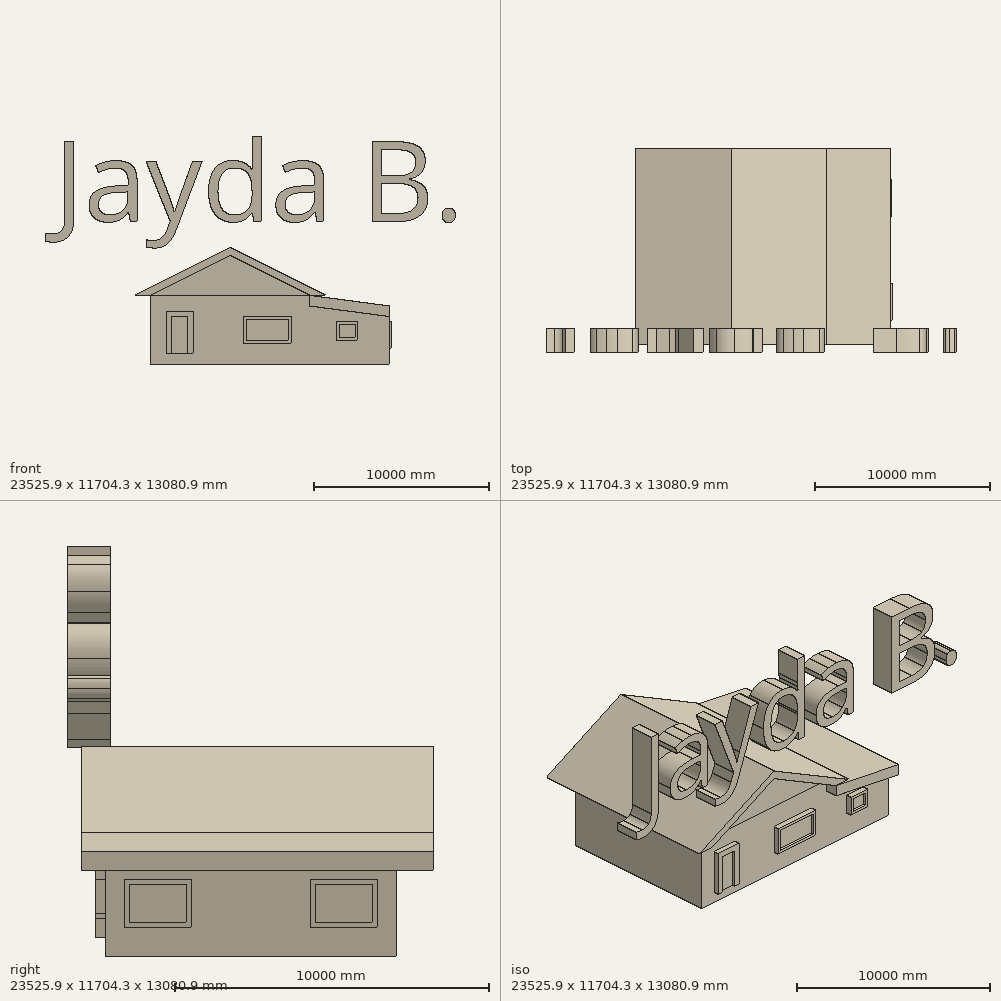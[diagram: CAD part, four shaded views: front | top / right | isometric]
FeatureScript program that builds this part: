
annotation { "Feature Type Name" : "Feature", "Feature Type Description" : "" }
export const myFeature = defineFeature(function(context is Context, id is Id, definition is map)
    precondition{}
    {
        {
            var Q0;
            Q0=qCreatedBy(makeId("Front.planeOp"),FACE);
            var sketch = newSketch(context, id + "F0", { "sketchPlane" : qUnion([Q0])});
            skLineSegment(sketch, "E0", {"start": v(0, 0) * mm, "end": v(-4572, 0) * mm});
            skLineSegment(sketch, "E1", {"start": v(0, 0) * mm, "end": v(4572, 0) * mm});
            skLineSegment(sketch, "E2", {"start": v(0, 0) * mm, "end": v(0, 2286) * mm});
            skLineSegment(sketch, "E3", {"start": v(-4572, 0) * mm, "end": v(0, 2286) * mm});
            skLineSegment(sketch, "E4", {"start": v(4572, 0) * mm, "end": v(0, 2286) * mm});
            skLineSegment(sketch, "E5", {"start": v(4572, 0) * mm, "end": v(5486.4, 0) * mm});
            skLineSegment(sketch, "E6", {"start": v(-4572, 0) * mm, "end": v(-5486.4, 0) * mm});
            skLineSegment(sketch, "E7", {"start": v(0, 2286) * mm, "end": v(0, 2743.2) * mm});
            skLineSegment(sketch, "E8", {"start": v(-5486.4, 0) * mm, "end": v(0, 2743.2) * mm});
            skLineSegment(sketch, "E9", {"start": v(5486.4, 0) * mm, "end": v(0, 2743.2) * mm});
            skLineSegment(sketch, "E10", {"start": v(-4572, 0) * mm, "end": v(-4572, -3352.8) * mm});
            skLineSegment(sketch, "E11", {"start": v(4572, 0) * mm, "end": v(4572, -3352.8) * mm});
            skLineSegment(sketch, "E12", {"start": v(4572, 0) * mm, "end": v(9144, -603.27) * mm});
            skLineSegment(sketch, "E13", {"start": v(-4572, -3352.8) * mm, "end": v(4572, -3352.8) * mm});
            skLineSegment(sketch, "E14", {"start": v(-4572, -3352.8) * mm, "end": v(-4572, -3962.4) * mm});
            skLineSegment(sketch, "E15", {"start": v(4572, -3352.8) * mm, "end": v(4572, -3962.4) * mm});
            skLineSegment(sketch, "E16", {"start": v(-4572, -3962.4) * mm, "end": v(4572, -3962.4) * mm});
            skLineSegment(sketch, "E17", {"start": v(-2438.4, -3352.8) * mm, "end": v(-2133.6, -3352.8) * mm});
            skLineSegment(sketch, "E18", {"start": v(-2438.4, -3352.8) * mm, "end": v(-2438.4, -1219.2) * mm});
            skLineSegment(sketch, "E19", {"start": v(-3657.6, -3352.8) * mm, "end": v(-3352.8, -3352.8) * mm});
            skLineSegment(sketch, "E20", {"start": v(-3352.8, -3352.8) * mm, "end": v(-3352.8, -1219.2) * mm});
            skLineSegment(sketch, "E21", {"start": v(-3352.8, -1219.2) * mm, "end": v(-2438.4, -1219.2) * mm});
            skLineSegment(sketch, "E22.0", {"start": v(-2133.6, -3352.8) * mm, "end": v(-2133.6, -914.4) * mm});
            skLineSegment(sketch, "E22.1", {"start": v(-3657.6, -914.4) * mm, "end": v(-2133.6, -914.4) * mm});
            skLineSegment(sketch, "E22.2", {"start": v(-3657.6, -3352.8) * mm, "end": v(-3657.6, -914.4) * mm});
            skLineSegment(sketch, "E23", {"start": v(9144, -603.27) * mm, "end": v(9144, -3346.47) * mm});
            skLineSegment(sketch, "E24", {"start": v(4572, -609.6) * mm, "end": v(9144, -1212.87) * mm});
            skLineSegment(sketch, "E25", {"start": v(9144, -3352.8) * mm, "end": v(9144, -3346.47) * mm});
            skLineSegment(sketch, "E26", {"start": v(4572, -3352.8) * mm, "end": v(9144, -3346.47) * mm});
            skLineSegment(sketch, "E27", {"start": v(4572, -3962.4) * mm, "end": v(9144, -3956.07) * mm});
            skLineSegment(sketch, "E28", {"start": v(9144, -3956.07) * mm, "end": v(9144, -3346.47) * mm});
            skLineSegment(sketch, "E29.bottom", {"start": v(6248.4, -1672.6) * mm, "end": v(7162.8, -1672.6) * mm});
            skLineSegment(sketch, "E29.top", {"start": v(6248.4, -2434.6) * mm, "end": v(7162.8, -2434.6) * mm});
            skLineSegment(sketch, "E29.left", {"start": v(6248.4, -1672.6) * mm, "end": v(6248.4, -2434.6) * mm});
            skLineSegment(sketch, "E29.right", {"start": v(7162.8, -1672.6) * mm, "end": v(7162.8, -2434.6) * mm});
            skLineSegment(sketch, "E30.0", {"start": v(6096, -1520.2) * mm, "end": v(7315.2, -1520.2) * mm});
            skLineSegment(sketch, "E30.1", {"start": v(6096, -1520.2) * mm, "end": v(6096, -2587) * mm});
            skLineSegment(sketch, "E30.2", {"start": v(6096, -2587) * mm, "end": v(7315.2, -2587) * mm});
            skLineSegment(sketch, "E30.3", {"start": v(7315.2, -1520.2) * mm, "end": v(7315.2, -2587) * mm});
            skLineSegment(sketch, "E31.bottom", {"start": v(914.4, -1371.6) * mm, "end": v(3352.8, -1371.6) * mm});
            skLineSegment(sketch, "E31.top", {"start": v(914.4, -2590.8) * mm, "end": v(3352.8, -2590.8) * mm});
            skLineSegment(sketch, "E31.left", {"start": v(914.4, -1371.6) * mm, "end": v(914.4, -2590.8) * mm});
            skLineSegment(sketch, "E31.right", {"start": v(3352.8, -1371.6) * mm, "end": v(3352.8, -2590.8) * mm});
            skLineSegment(sketch, "E32.0", {"start": v(762, -1219.2) * mm, "end": v(3505.2, -1219.2) * mm});
            skLineSegment(sketch, "E32.1", {"start": v(762, -1219.2) * mm, "end": v(762, -2743.2) * mm});
            skLineSegment(sketch, "E32.2", {"start": v(762, -2743.2) * mm, "end": v(3505.2, -2743.2) * mm});
            skLineSegment(sketch, "E32.3", {"start": v(3505.2, -1219.2) * mm, "end": v(3505.2, -2743.2) * mm});
            skLineSegment(sketch, "E33", {"start": v(-3657.6, -3352.8) * mm, "end": v(-2133.6, -3352.8) * mm});
            skText(sketch, "E34", { "text": "Jayda B.", "fontName": "OpenSans-Regular.ttf"});
            const initialGuessF0  = {"E34": [-10.1014, 4.25261, 1, 0, 4.61073]};
            skSetInitialGuess(sketch, initialGuessF0);
            skSolve(sketch);
        }
        {
            var Q0;
            Q0=makeQuery(id+"F0.imprint","IMPRINT",FACE,{"disambiguationData":[TD([[makeQuery(id+"F0.imprint","IMPRINT",EDGE,{"derivedFrom":sQuery(id+"F0.wireOp",EDGE,"E3")}),1.0]])]});
            var Q1;
            Q1=makeQuery(id+"F0.imprint","IMPRINT",FACE,{"disambiguationData":[TD([[makeQuery(id+"F0.imprint","IMPRINT",EDGE,{"derivedFrom":sQuery(id+"F0.wireOp",EDGE,"E4")}),-1.0]])]});
            extrude(context, id + "F1", {"entities" : qUnion([Q0, Q1]), "depth" : 914.4 * mm, "offsetDistance" : 30.48 * mm, "hasSecondDirection" : true, "secondDirectionOppositeDirection" : true, "secondDirectionDepth" : 12192 * mm});
        }
        {
            var Q0;
            Q0=makeQuery(id+"F0.imprint","IMPRINT",FACE,{"disambiguationData":[TD([[makeQuery(id+"F0.imprint","IMPRINT",EDGE,{"derivedFrom":sQuery(id+"F0.wireOp",EDGE,"E0")}),-1.0]])]});
            var Q1;
            Q1=makeQuery(id+"F0.imprint","IMPRINT",FACE,{"disambiguationData":[TD([[makeQuery(id+"F0.imprint","IMPRINT",EDGE,{"derivedFrom":sQuery(id+"F0.wireOp",EDGE,"E1")}),1.0]])]});
            extrude(context, id + "F2", {"entities" : qUnion([Q0, Q1]), "operationType" : NewBodyOperationType.ADD, "depth" : 152.4 * mm, "offsetDistance" : 30.48 * mm, "hasSecondDirection" : true, "secondDirectionOppositeDirection" : true, "secondDirectionDepth" : 9144 * mm});
        }
        {
            var Q0;
            {var subQ0=sQuery(id+"F0.wireOp",EDGE,"E12");Q0=makeQuery(id+"F0.imprint","IMPRINT",FACE,{"disambiguationData":[TD([[makeQuery(id+"F0.imprint","IMPRINT",EDGE,{"derivedFrom":subQ0}),-1.0]])]});}
            extrude(context, id + "F3", {"entities" : qUnion([Q0]), "depth" : 914.4 * mm, "offsetDistance" : 30.48 * mm, "hasSecondDirection" : true, "secondDirectionOppositeDirection" : true, "secondDirectionDepth" : 12192 * mm});
        }
        {
            var Q0;
            Q0=makeQuery(id+"F0.imprint","IMPRINT",FACE,{"disambiguationData":[TD([[makeQuery(id+"F0.imprint","IMPRINT",EDGE,{"derivedFrom":sQuery(id+"F0.wireOp",EDGE,"E0")}),1.0]])]});
            var Q1;
            {var subQ1=sQuery(id+"F0.wireOp",EDGE,"E24");Q1=makeQuery(id+"F0.imprint","IMPRINT",FACE,{"disambiguationData":[TD([[makeQuery(id+"F0.imprint","IMPRINT",EDGE,{"derivedFrom":subQ1}),-1.0]])]});}
            extrude(context, id + "F4", {"entities" : qUnion([Q0, Q1]), "depth" : 152.4 * mm, "offsetDistance" : 30.48 * mm, "hasSecondDirection" : true, "secondDirectionOppositeDirection" : true, "secondDirectionDepth" : 9144 * mm});
        }
        {
            var Q0;
            Q0=makeQuery(id+"F0.imprint","IMPRINT",FACE,{"disambiguationData":[TD([[makeQuery(id+"F0.imprint","IMPRINT",EDGE,{"derivedFrom":sQuery(id+"F0.wireOp",EDGE,"E17")}),1.0]])]});
            var Q1;
            Q1=makeQuery(id+"F0.imprint","IMPRINT",FACE,{"disambiguationData":[TD([[makeQuery(id+"F0.imprint","IMPRINT",EDGE,{"derivedFrom":sQuery(id+"F0.wireOp",EDGE,"E29.bottom")}),1.0]])]});
            var Q2;
            {var subQ1=sQuery(id+"F0.wireOp",EDGE,"E14");Q2=makeQuery(id+"F0.imprint","IMPRINT",FACE,{"disambiguationData":[TD([[makeQuery(id+"F0.imprint","IMPRINT",EDGE,{"derivedFrom":subQ1}),1.0]])]});}
            var Q3;
            Q3=makeQuery(id+"F0.imprint","IMPRINT",FACE,{"disambiguationData":[TD([[makeQuery(id+"F0.imprint","IMPRINT",EDGE,{"derivedFrom":sQuery(id+"F0.wireOp",EDGE,"E15")}),1.0]])]});
            var Q4;
            {var subQ2=sQuery(id+"F0.wireOp",EDGE,"E18");Q4=makeQuery(id+"F0.imprint","IMPRINT",FACE,{"disambiguationData":[TD([[makeQuery(id+"F0.imprint","IMPRINT",EDGE,{"derivedFrom":subQ2}),-1.0]])]});}
            var Q5;
            Q5=makeQuery(id+"F0.imprint","IMPRINT",FACE,{"disambiguationData":[TD([[makeQuery(id+"F0.imprint","IMPRINT",EDGE,{"derivedFrom":sQuery(id+"F0.wireOp",EDGE,"E31.bottom")}),1.0]])]});
            extrude(context, id + "F5", {"entities" : qUnion([Q0, Q1, Q2, Q3, Q4, Q5]), "operationType" : NewBodyOperationType.ADD, "depth" : 152.4 * mm, "offsetDistance" : 30.48 * mm, "hasSecondDirection" : true, "secondDirectionOppositeDirection" : true, "secondDirectionDepth" : 9144 * mm});
        }
        {
            var Q0;
            Q0=makeQuery(id+"F0.imprint","IMPRINT",FACE,{"disambiguationData":[TD([[makeQuery(id+"F0.imprint","IMPRINT",EDGE,{"derivedFrom":sQuery(id+"F0.wireOp",EDGE,"E15")}),1.0]])]});
            extrude(context, id + "F6", {"entities" : qUnion([Q0]), "operationType" : NewBodyOperationType.ADD, "depth" : 152.4 * mm, "offsetDistance" : 30.48 * mm, "hasSecondDirection" : true, "secondDirectionOppositeDirection" : true, "secondDirectionDepth" : 152.4 * mm});
        }
        {
            var Q0;
            Q0=makeQuery(id+"F0.imprint","IMPRINT",FACE,{"disambiguationData":[TD([[makeQuery(id+"F0.imprint","IMPRINT",EDGE,{"derivedFrom":sQuery(id+"F0.wireOp",EDGE,"E31.bottom")}),-1.0]])]});
            var Q1;
            {var subQ0=sQuery(id+"F0.wireOp",EDGE,"E18");Q1=makeQuery(id+"F0.imprint","IMPRINT",FACE,{"disambiguationData":[TD([[makeQuery(id+"F0.imprint","IMPRINT",EDGE,{"derivedFrom":subQ0}),1.0]])]});}
            var Q2;
            Q2=makeQuery(id+"F0.imprint","IMPRINT",FACE,{"disambiguationData":[TD([[makeQuery(id+"F0.imprint","IMPRINT",EDGE,{"derivedFrom":sQuery(id+"F0.wireOp",EDGE,"E29.bottom")}),-1.0]])]});
            extrude(context, id + "F7", {"entities" : qUnion([Q0, Q1, Q2]), "operationType" : NewBodyOperationType.ADD, "depth" : 152.4 * mm, "offsetDistance" : 30.48 * mm, "hasSecondDirection" : true, "secondDirectionOppositeDirection" : true, "secondDirectionDepth" : 152.4 * mm});
        }
        {
            var Q0;
            Q0=makeQuery(id+"F3.opExtrude","CAP_FACE",FACE,{"disambiguationData":[OSD([sQuery(id+"F0.wireOp",EDGE,"E11"),sQuery(id+"F0.wireOp",EDGE,"E12"),sQuery(id+"F0.wireOp",EDGE,"E23"),sQuery(id+"F0.wireOp",EDGE,"E24")])],"isStart":true});
            extrude(context, id + "F8", {"entities" : qUnion([Q0]), "operationType" : NewBodyOperationType.REMOVE, "oppositeDirection" : true, "depth" : 1868.42 * mm, "offsetDistance" : 30.48 * mm});
        }
        {
            var Q0;
            Q0=makeQuery(id+"F8.boolean.opBoolean","COPY",FACE,{"derivedFrom":makeQuery(id+"F8.opExtrude","CAP_FACE",FACE,{"disambiguationData":[OSD([sQuery(id+"F0.wireOp",EDGE,"E11"),sQuery(id+"F0.wireOp",EDGE,"E12"),sQuery(id+"F0.wireOp",EDGE,"E23"),sQuery(id+"F0.wireOp",EDGE,"E24")])],"isStart":false})});
            extrude(context, id + "F9", {"entities" : qUnion([Q0]), "operationType" : NewBodyOperationType.ADD, "oppositeDirection" : true, "depth" : 463.3 * mm, "offsetDistance" : 30.48 * mm});
        }
        {
            var Q0;
            Q0=makeQuery(id+"F1.opExtrude","CAP_FACE",FACE,{"disambiguationData":[OSD([sQuery(id+"F0.wireOp",EDGE,"E3"),sQuery(id+"F0.wireOp",EDGE,"E4"),sQuery(id+"F0.wireOp",EDGE,"E5"),sQuery(id+"F0.wireOp",EDGE,"E6"),sQuery(id+"F0.wireOp",EDGE,"E8"),sQuery(id+"F0.wireOp",EDGE,"E9")])],"isStart":true});
            extrude(context, id + "F10", {"entities" : qUnion([Q0]), "operationType" : NewBodyOperationType.ADD, "oppositeDirection" : true, "depth" : 2011.68 * mm, "offsetDistance" : 30.48 * mm});
        }
        {
            var Q0;
            Q0=makeQuery(id+"F1.opExtrude","CAP_FACE",FACE,{"disambiguationData":[OSD([sQuery(id+"F0.wireOp",EDGE,"E3"),sQuery(id+"F0.wireOp",EDGE,"E4"),sQuery(id+"F0.wireOp",EDGE,"E5"),sQuery(id+"F0.wireOp",EDGE,"E6"),sQuery(id+"F0.wireOp",EDGE,"E8"),sQuery(id+"F0.wireOp",EDGE,"E9")])],"isStart":true});
            extrude(context, id + "F11", {"entities" : qUnion([Q0]), "operationType" : NewBodyOperationType.ADD, "oppositeDirection" : true, "depth" : 1798.32 * mm, "offsetDistance" : 30.48 * mm});
        }
        {
            var Q0;
            Q0=makeQuery(id+"F1.opExtrude","CAP_FACE",FACE,{"disambiguationData":[OSD([sQuery(id+"F0.wireOp",EDGE,"E3"),sQuery(id+"F0.wireOp",EDGE,"E4"),sQuery(id+"F0.wireOp",EDGE,"E5"),sQuery(id+"F0.wireOp",EDGE,"E6"),sQuery(id+"F0.wireOp",EDGE,"E8"),sQuery(id+"F0.wireOp",EDGE,"E9")])],"isStart":true});
            extrude(context, id + "F12", {"entities" : qUnion([Q0]), "operationType" : NewBodyOperationType.ADD, "oppositeDirection" : true, "depth" : 2133.6 * mm, "offsetDistance" : 30.48 * mm});
        }
        {
            var Q0;
            Q0=makeQuery(id+"F1.opExtrude","CAP_FACE",FACE,{"disambiguationData":[OSD([sQuery(id+"F0.wireOp",EDGE,"E3"),sQuery(id+"F0.wireOp",EDGE,"E4"),sQuery(id+"F0.wireOp",EDGE,"E5"),sQuery(id+"F0.wireOp",EDGE,"E6"),sQuery(id+"F0.wireOp",EDGE,"E8"),sQuery(id+"F0.wireOp",EDGE,"E9")])],"isStart":true});
            extrude(context, id + "F13", {"entities" : qUnion([Q0]), "operationType" : NewBodyOperationType.ADD, "oppositeDirection" : true, "depth" : 2773.68 * mm, "offsetDistance" : 30.48 * mm});
        }
        {
            var Q0;
            Q0=makeQuery(id+"F1.opExtrude","CAP_FACE",FACE,{"disambiguationData":[OSD([sQuery(id+"F0.wireOp",EDGE,"E3"),sQuery(id+"F0.wireOp",EDGE,"E4"),sQuery(id+"F0.wireOp",EDGE,"E5"),sQuery(id+"F0.wireOp",EDGE,"E6"),sQuery(id+"F0.wireOp",EDGE,"E8"),sQuery(id+"F0.wireOp",EDGE,"E9")])],"isStart":true});
            extrude(context, id + "F14", {"entities" : qUnion([Q0]), "operationType" : NewBodyOperationType.ADD, "oppositeDirection" : true, "depth" : 1706.88 * mm, "offsetDistance" : 30.48 * mm});
        }
        {
            var Q0;
            Q0=makeQuery(id+"F1.opExtrude","CAP_FACE",FACE,{"disambiguationData":[OSD([sQuery(id+"F0.wireOp",EDGE,"E3"),sQuery(id+"F0.wireOp",EDGE,"E4"),sQuery(id+"F0.wireOp",EDGE,"E5"),sQuery(id+"F0.wireOp",EDGE,"E6"),sQuery(id+"F0.wireOp",EDGE,"E8"),sQuery(id+"F0.wireOp",EDGE,"E9")])],"isStart":true});
            extrude(context, id + "F15", {"entities" : qUnion([Q0]), "operationType" : NewBodyOperationType.ADD, "oppositeDirection" : true, "depth" : 1828.8 * mm, "offsetDistance" : 30.48 * mm});
        }
        {
            var Q0;
            Q0=makeQuery(id+"F1.opExtrude","CAP_FACE",FACE,{"disambiguationData":[OSD([sQuery(id+"F0.wireOp",EDGE,"E3"),sQuery(id+"F0.wireOp",EDGE,"E4"),sQuery(id+"F0.wireOp",EDGE,"E5"),sQuery(id+"F0.wireOp",EDGE,"E6"),sQuery(id+"F0.wireOp",EDGE,"E8"),sQuery(id+"F0.wireOp",EDGE,"E9")])],"isStart":true});
            extrude(context, id + "F16", {"entities" : qUnion([Q0]), "operationType" : NewBodyOperationType.REMOVE, "oppositeDirection" : true, "depth" : 1859.28 * mm, "offsetDistance" : 30.48 * mm});
        }
        {
            var Q0;
            Q0=makeQuery(id+"F0.imprint","IMPRINT",FACE,{"disambiguationData":[TD([[makeQuery(id+"F0.imprint","IMPRINT",EDGE,{"derivedFrom":sQuery(id+"F0.wireOp",EDGE,"E31.bottom")}),-1.0]])]});
            var Q1;
            {var subQ0=sQuery(id+"F0.wireOp",EDGE,"E18");Q1=makeQuery(id+"F0.imprint","IMPRINT",FACE,{"disambiguationData":[TD([[makeQuery(id+"F0.imprint","IMPRINT",EDGE,{"derivedFrom":subQ0}),1.0]])]});}
            var Q2;
            Q2=makeQuery(id+"F0.imprint","IMPRINT",FACE,{"disambiguationData":[TD([[makeQuery(id+"F0.imprint","IMPRINT",EDGE,{"derivedFrom":sQuery(id+"F0.wireOp",EDGE,"E29.bottom")}),-1.0]])]});
            extrude(context, id + "F17", {"entities" : qUnion([Q0, Q1, Q2]), "operationType" : NewBodyOperationType.ADD, "depth" : 304.8 * mm, "offsetDistance" : 30.48 * mm});
        }
        {
            var Q0;
            {var subQ2=sQuery(id+"F0.wireOp",EDGE,"E18");Q0=makeQuery(id+"F0.imprint","IMPRINT",FACE,{"disambiguationData":[TD([[makeQuery(id+"F0.imprint","IMPRINT",EDGE,{"derivedFrom":subQ2}),-1.0]])]});}
            var Q1;
            Q1=makeQuery(id+"F0.imprint","IMPRINT",FACE,{"disambiguationData":[TD([[makeQuery(id+"F0.imprint","IMPRINT",EDGE,{"derivedFrom":sQuery(id+"F0.wireOp",EDGE,"E31.bottom")}),1.0]])]});
            var Q2;
            Q2=makeQuery(id+"F0.imprint","IMPRINT",FACE,{"disambiguationData":[TD([[makeQuery(id+"F0.imprint","IMPRINT",EDGE,{"derivedFrom":sQuery(id+"F0.wireOp",EDGE,"E29.bottom")}),1.0]])]});
            extrude(context, id + "F18", {"entities" : qUnion([Q0, Q1, Q2]), "operationType" : NewBodyOperationType.ADD, "depth" : 457.2 * mm, "offsetDistance" : 30.48 * mm});
        }
        {
            var Q0;
            Q0=makeQuery(id+"F5.boolean.opBoolean","MERGE",FACE,{"derivedFrom":[makeQuery(id+"F4.opExtrude","SWEPT_FACE",FACE,{"disambiguationData":[OSD([sQuery(id+"F0.wireOp",EDGE,"E23")])]}),makeQuery(id+"F5.opExtrude","SWEPT_FACE",FACE,{"disambiguationData":[OSD([sQuery(id+"F0.wireOp",EDGE,"E28")])]})]});
            var sketch = newSketch(context, id + "F19", { "sketchPlane" : qUnion([Q0])});
            skLineSegment(sketch, "E35.bottom", {"start": v(609.6, -1670.07) * mm, "end": v(2438.4, -1670.07) * mm});
            skLineSegment(sketch, "E35.top", {"start": v(609.6, -2889.27) * mm, "end": v(2438.4, -2889.27) * mm});
            skLineSegment(sketch, "E35.left", {"start": v(609.6, -1670.07) * mm, "end": v(609.6, -2889.27) * mm});
            skLineSegment(sketch, "E35.right", {"start": v(2438.4, -1670.07) * mm, "end": v(2438.4, -2889.27) * mm});
            skLineSegment(sketch, "E36.0", {"start": v(457.2, -1517.67) * mm, "end": v(2590.8, -1517.67) * mm});
            skLineSegment(sketch, "E36.1", {"start": v(457.2, -1517.67) * mm, "end": v(457.2, -3041.67) * mm});
            skLineSegment(sketch, "E36.2", {"start": v(457.2, -3041.67) * mm, "end": v(2590.8, -3041.67) * mm});
            skLineSegment(sketch, "E36.3", {"start": v(2590.8, -1517.67) * mm, "end": v(2590.8, -3041.67) * mm});
            skLineSegment(sketch, "E37.bottom", {"start": v(6553.2, -1670.07) * mm, "end": v(8382, -1670.07) * mm});
            skLineSegment(sketch, "E37.top", {"start": v(6553.2, -2889.27) * mm, "end": v(8382, -2889.27) * mm});
            skLineSegment(sketch, "E37.left", {"start": v(6553.2, -1670.07) * mm, "end": v(6553.2, -2889.27) * mm});
            skLineSegment(sketch, "E37.right", {"start": v(8382, -1670.07) * mm, "end": v(8382, -2889.27) * mm});
            skLineSegment(sketch, "E38.0", {"start": v(6400.8, -1517.67) * mm, "end": v(8534.4, -1517.67) * mm});
            skLineSegment(sketch, "E38.1", {"start": v(6400.8, -1517.67) * mm, "end": v(6400.8, -3041.67) * mm});
            skLineSegment(sketch, "E38.2", {"start": v(6400.8, -3041.67) * mm, "end": v(8534.4, -3041.67) * mm});
            skLineSegment(sketch, "E38.3", {"start": v(8534.4, -1517.67) * mm, "end": v(8534.4, -3041.67) * mm});
            skSolve(sketch);
        }
        {
            var Q0;
            Q0=makeQuery(id+"F19.imprint","IMPRINT",FACE,{"disambiguationData":[TD([[makeQuery(id+"F19.imprint","IMPRINT",EDGE,{"derivedFrom":sQuery(id+"F19.wireOp",EDGE,"E35.bottom")}),1.0]])]});
            var Q1;
            Q1=makeQuery(id+"F19.imprint","IMPRINT",FACE,{"disambiguationData":[TD([[makeQuery(id+"F19.imprint","IMPRINT",EDGE,{"derivedFrom":sQuery(id+"F19.wireOp",EDGE,"E37.bottom")}),1.0]])]});
            extrude(context, id + "F20", {"entities" : qUnion([Q0, Q1]), "operationType" : NewBodyOperationType.ADD, "depth" : 30.48 * mm, "offsetDistance" : 30.48 * mm});
        }
        {
            var Q0;
            Q0=makeQuery(id+"F20.opExtrude","CAP_FACE",FACE,{"disambiguationData":[OSD([sQuery(id+"F19.wireOp",EDGE,"E35.bottom"),sQuery(id+"F19.wireOp",EDGE,"E35.top"),sQuery(id+"F19.wireOp",EDGE,"E35.left"),sQuery(id+"F19.wireOp",EDGE,"E35.right"),sQuery(id+"F19.wireOp",EDGE,"E36.0"),sQuery(id+"F19.wireOp",EDGE,"E36.1"),sQuery(id+"F19.wireOp",EDGE,"E36.2"),sQuery(id+"F19.wireOp",EDGE,"E36.3")])],"isStart":false});
            var Q1;
            Q1=makeQuery(id+"F20.opExtrude","CAP_FACE",FACE,{"disambiguationData":[OSD([sQuery(id+"F19.wireOp",EDGE,"E37.bottom"),sQuery(id+"F19.wireOp",EDGE,"E37.top"),sQuery(id+"F19.wireOp",EDGE,"E37.left"),sQuery(id+"F19.wireOp",EDGE,"E37.right"),sQuery(id+"F19.wireOp",EDGE,"E38.0"),sQuery(id+"F19.wireOp",EDGE,"E38.1"),sQuery(id+"F19.wireOp",EDGE,"E38.2"),sQuery(id+"F19.wireOp",EDGE,"E38.3")])],"isStart":false});
            extrude(context, id + "F21", {"entities" : qUnion([Q0, Q1]), "operationType" : NewBodyOperationType.ADD, "depth" : 30.48 * mm, "offsetDistance" : 30.48 * mm, "hasSecondDirection" : true, "secondDirectionOppositeDirection" : true, "secondDirectionDepth" : 457.2 * mm});
        }
        {
            var Q0;
            Q0=makeQuery(id+"F20.boolean.opBoolean","SPLIT",FACE,{"disambiguationData":[TD([makeQuery(id+"F20.opExtrude","SWEPT_FACE",FACE,{"disambiguationData":[OSD([sQuery(id+"F19.wireOp",EDGE,"E35.bottom")])]})])],"derivedFrom":makeQuery(id+"F5.boolean.opBoolean","MERGE",FACE,{"derivedFrom":[makeQuery(id+"F4.opExtrude","SWEPT_FACE",FACE,{"disambiguationData":[OSD([sQuery(id+"F0.wireOp",EDGE,"E23")])]}),makeQuery(id+"F5.opExtrude","SWEPT_FACE",FACE,{"disambiguationData":[OSD([sQuery(id+"F0.wireOp",EDGE,"E28")])]})]})});
            var Q1;
            Q1=makeQuery(id+"F20.boolean.opBoolean","SPLIT",FACE,{"disambiguationData":[TD([makeQuery(id+"F20.opExtrude","SWEPT_FACE",FACE,{"disambiguationData":[OSD([sQuery(id+"F19.wireOp",EDGE,"E37.bottom")])]})])],"derivedFrom":makeQuery(id+"F5.boolean.opBoolean","MERGE",FACE,{"derivedFrom":[makeQuery(id+"F4.opExtrude","SWEPT_FACE",FACE,{"disambiguationData":[OSD([sQuery(id+"F0.wireOp",EDGE,"E23")])]}),makeQuery(id+"F5.opExtrude","SWEPT_FACE",FACE,{"disambiguationData":[OSD([sQuery(id+"F0.wireOp",EDGE,"E28")])]})]})});
            extrude(context, id + "F22", {"entities" : qUnion([Q0, Q1]), "operationType" : NewBodyOperationType.ADD, "depth" : 30.48 * mm, "offsetDistance" : 30.48 * mm, "hasSecondDirection" : true, "secondDirectionOppositeDirection" : true, "secondDirectionDepth" : 304.8 * mm});
        }
        {
            var Q0;
            Q0=makeQuery(id+"F19.imprint","IMPRINT",FACE,{"disambiguationData":[TD([[makeQuery(id+"F19.imprint","IMPRINT",EDGE,{"derivedFrom":sQuery(id+"F19.wireOp",EDGE,"E35.bottom")}),-1.0]])]});
            var Q1;
            Q1=makeQuery(id+"F19.imprint","IMPRINT",FACE,{"disambiguationData":[TD([[makeQuery(id+"F19.imprint","IMPRINT",EDGE,{"derivedFrom":sQuery(id+"F19.wireOp",EDGE,"E37.bottom")}),-1.0]])]});
            extrude(context, id + "F23", {"entities" : qUnion([Q0, Q1]), "operationType" : NewBodyOperationType.ADD, "depth" : 30.48 * mm, "offsetDistance" : 30.48 * mm, "hasSecondDirection" : true, "secondDirectionOppositeDirection" : true, "secondDirectionDepth" : 304.8 * mm});
        }
        {
            var Q0;
            Q0 = qSketchRegion(id + "F19", true);
            var Q1;
            Q1=makeQuery(id+"F21.opExtrude","CAP_FACE",FACE,{"disambiguationData":[OSD([sQuery(id+"F19.wireOp",EDGE,"E35.bottom"),sQuery(id+"F19.wireOp",EDGE,"E35.top"),sQuery(id+"F19.wireOp",EDGE,"E35.left"),sQuery(id+"F19.wireOp",EDGE,"E35.right"),sQuery(id+"F19.wireOp",EDGE,"E36.0"),sQuery(id+"F19.wireOp",EDGE,"E36.1"),sQuery(id+"F19.wireOp",EDGE,"E36.2"),sQuery(id+"F19.wireOp",EDGE,"E36.3")])],"isStart":false});
            extrude(context, id + "F24", {"entities" : qUnion([Q0, Q1]), "operationType" : NewBodyOperationType.ADD, "depth" : 30.48 * mm, "offsetDistance" : 30.48 * mm, "hasSecondDirection" : true, "secondDirectionOppositeDirection" : true, "secondDirectionDepth" : 457.2 * mm});
        }
        {
            var Q0;
            Q0=makeQuery(id+"F0.imprint","IMPRINT",FACE,{"disambiguationData":[TD([[makeQuery(id+"F0.imprint","IMPRINT",EDGE,{"derivedFrom":sQuery(id+"F0.wireOp",EDGE,"E34.sketch_text.stroke-77")}),-1.0]])]});
            var Q1;
            Q1=makeQuery(id+"F0.imprint","IMPRINT",FACE,{"disambiguationData":[TD([[makeQuery(id+"F0.imprint","IMPRINT",EDGE,{"derivedFrom":sQuery(id+"F0.wireOp",EDGE,"E34.sketch_text.stroke-104")}),-1.0]])]});
            var Q2;
            Q2=makeQuery(id+"F0.imprint","IMPRINT",FACE,{"disambiguationData":[TD([[makeQuery(id+"F0.imprint","IMPRINT",EDGE,{"derivedFrom":sQuery(id+"F0.wireOp",EDGE,"E34.sketch_text.stroke-53")}),-1.0]])]});
            var Q3;
            Q3=makeQuery(id+"F0.imprint","IMPRINT",FACE,{"disambiguationData":[TD([[makeQuery(id+"F0.imprint","IMPRINT",EDGE,{"derivedFrom":sQuery(id+"F0.wireOp",EDGE,"E34.sketch_text.stroke-37")}),-1.0]])]});
            var Q4;
            Q4=makeQuery(id+"F0.imprint","IMPRINT",FACE,{"disambiguationData":[TD([[makeQuery(id+"F0.imprint","IMPRINT",EDGE,{"derivedFrom":sQuery(id+"F0.wireOp",EDGE,"E34.sketch_text.stroke-10")}),-1.0]])]});
            var Q5;
            Q5=makeQuery(id+"F0.imprint","IMPRINT",FACE,{"disambiguationData":[TD([[makeQuery(id+"F0.imprint","IMPRINT",EDGE,{"derivedFrom":sQuery(id+"F0.wireOp",EDGE,"E34.sketch_text.stroke-0")}),-1.0]])]});
            var Q6;
            Q6=makeQuery(id+"F0.imprint","IMPRINT",FACE,{"disambiguationData":[TD([[makeQuery(id+"F0.imprint","IMPRINT",EDGE,{"derivedFrom":sQuery(id+"F0.wireOp",EDGE,"E34.sketch_text.stroke-129")}),-1.0]])]});
            extrude(context, id + "F25", {"entities" : qUnion([Q0, Q1, Q2, Q3, Q4, Q5, Q6]), "depth" : 1371.6 * mm, "offsetDistance" : 30.48 * mm});
        }
    });
